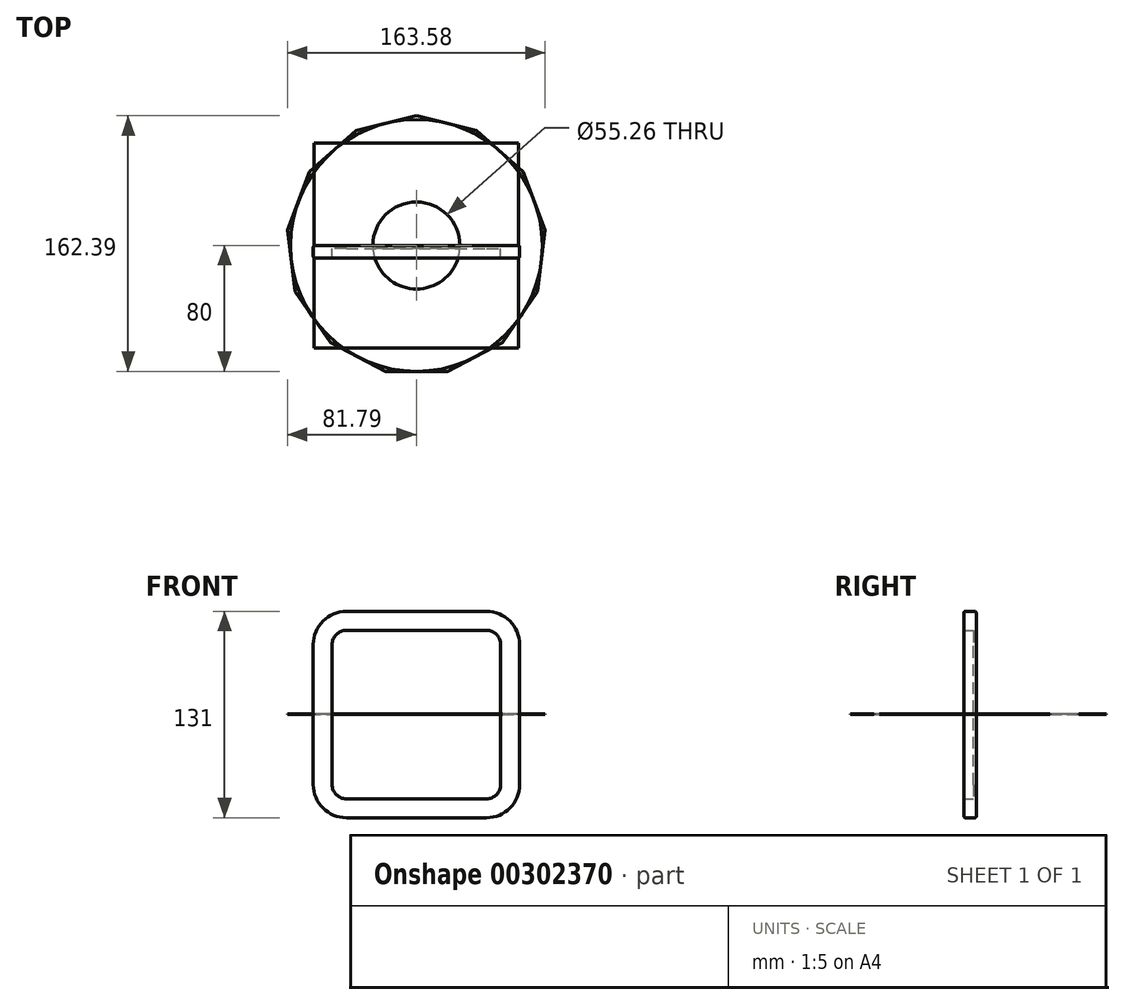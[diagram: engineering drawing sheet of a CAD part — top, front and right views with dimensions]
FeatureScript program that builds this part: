
annotation { "Feature Type Name" : "Feature", "Feature Type Description" : "" }
export const myFeature = defineFeature(function(context is Context, id is Id, definition is map)
    precondition{}
    {
        {
            var Q0;
            Q0=qCreatedBy(makeId("Front.planeOp"),FACE);
            var sketch = newSketch(context, id + "F0", { "sketchPlane" : qUnion([Q0])});
            skLineSegment(sketch, "E0.bottom", {"start": v(44.5, 53.5) * mm, "end": v(-44.5, 53.5) * mm});
            skLineSegment(sketch, "E0.top", {"start": v(44.5, -53.5) * mm, "end": v(-44.5, -53.5) * mm});
            skLineSegment(sketch, "E0.left", {"start": v(53.5, 44.5) * mm, "end": v(53.5, -44.5) * mm});
            skLineSegment(sketch, "E0.right", {"start": v(-53.5, 44.5) * mm, "end": v(-53.5, -44.5) * mm});
            skPoint(sketch, "E0.middle", {"position": v(0, 0) * mm});
            skPoint(sketch, "E1.visualSharp", {"position": v(-53.5, 53.5) * mm});
            skArc(sketch, "E1.filletArc", {"start": v(-44.5, 53.5) * mm, "mid": v(-50.86, 50.86) * mm, "end": v(-53.5, 44.5) * mm});
            skPoint(sketch, "E2.visualSharp", {"position": v(53.5, 53.5) * mm});
            skArc(sketch, "E2.filletArc", {"start": v(53.5, 44.5) * mm, "mid": v(50.86, 50.86) * mm, "end": v(44.5, 53.5) * mm});
            skPoint(sketch, "E3.visualSharp", {"position": v(-53.5, -53.5) * mm});
            skArc(sketch, "E3.filletArc", {"start": v(-53.5, -44.5) * mm, "mid": v(-50.86, -50.86) * mm, "end": v(-44.5, -53.5) * mm});
            skPoint(sketch, "E4.visualSharp", {"position": v(53.5, -53.5) * mm});
            skArc(sketch, "E4.filletArc", {"start": v(44.5, -53.5) * mm, "mid": v(50.86, -50.86) * mm, "end": v(53.5, -44.5) * mm});
            skLineSegment(sketch, "E5.0", {"start": v(65.5, 44.5) * mm, "end": v(65.5, -44.5) * mm});
            skArc(sketch, "E5.1", {"start": v(44.5, -65.5) * mm, "mid": v(59.35, -59.35) * mm, "end": v(65.5, -44.5) * mm});
            skArc(sketch, "E5.2", {"start": v(65.5, 44.5) * mm, "mid": v(59.35, 59.35) * mm, "end": v(44.5, 65.5) * mm});
            skLineSegment(sketch, "E5.3", {"start": v(44.5, -65.5) * mm, "end": v(-44.5, -65.5) * mm});
            skLineSegment(sketch, "E5.4", {"start": v(44.5, 65.5) * mm, "end": v(-44.5, 65.5) * mm});
            skArc(sketch, "E5.5", {"start": v(-44.5, 65.5) * mm, "mid": v(-59.35, 59.35) * mm, "end": v(-65.5, 44.5) * mm});
            skLineSegment(sketch, "E5.6", {"start": v(-65.5, 44.5) * mm, "end": v(-65.5, -44.5) * mm});
            skArc(sketch, "E5.7", {"start": v(-65.5, -44.5) * mm, "mid": v(-59.35, -59.35) * mm, "end": v(-44.5, -65.5) * mm});
            skSolve(sketch);
        }
        {
            var Q0;
            Q0 = qSketchRegion(id + "F0", true);
            var Q1;
            Q1=makeQuery(id+"F0.imprint","IMPRINT",FACE,{"disambiguationData":[TD([[makeQuery(id+"F0.imprint","IMPRINT",EDGE,{"derivedFrom":sQuery(id+"F0.wireOp",EDGE,"E0.bottom")}),1.0]])]});
            extrude(context, id + "F1", {"entities" : qUnion([Q0, Q1]), "depth" : 2 * mm});
        }
        {
            var Q0;
            Q0=makeQuery(id+"F0.imprint","IMPRINT",FACE,{"disambiguationData":[TD([[makeQuery(id+"F0.imprint","IMPRINT",EDGE,{"derivedFrom":sQuery(id+"F0.wireOp",EDGE,"E0.bottom")}),-1.0]])]});
            extrude(context, id + "F2", {"entities" : qUnion([Q0]), "operationType" : NewBodyOperationType.ADD, "depth" : 8 * mm});
        }
        {
            var Q0;
            Q0=makeQuery(id+"F1.opExtrude","CAP_EDGE",EDGE,{"disambiguationData":[OSD([sQuery(id+"F0.wireOp",EDGE,"E5.3")])],"isStart":true});
            var Q1;
            Q1=makeQuery(id+"F2.opExtrude","CAP_EDGE",EDGE,{"disambiguationData":[OSD([sQuery(id+"F0.wireOp",EDGE,"E5.3")])],"isStart":false});
            fillet(context, id + "F3", {"entities" : qUnion([Q0, Q1]), "radius" : 1 * mm, "tangentPropagation" : true, "allowEdgeOverflow" : false});
        }
        {
            var Q0;
            Q0=qCreatedBy(makeId("Top.planeOp"),FACE);
            var sketch = newSketch(context, id + "F4", { "sketchPlane" : qUnion([Q0])});
            skCircle(sketch, "E6.cCircle", {"center": v(0, 0) * mm, "radius": 80 * mm, "construction": true});
            skLineSegment(sketch, "E6.0", {"start": v(38.3, 72.96) * mm, "end": v(67.8, 46.8) * mm});
            skLineSegment(sketch, "E6.1", {"start": v(67.8, 46.8) * mm, "end": v(81.8, 9.93) * mm});
            skLineSegment(sketch, "E6.2", {"start": v(81.8, 9.93) * mm, "end": v(77.04, -29.22) * mm});
            skLineSegment(sketch, "E6.3", {"start": v(77.04, -29.22) * mm, "end": v(54.64, -61.67) * mm});
            skLineSegment(sketch, "E6.4", {"start": v(54.64, -61.67) * mm, "end": v(19.72, -80) * mm});
            skLineSegment(sketch, "E6.5", {"start": v(19.72, -80) * mm, "end": v(-19.72, -80) * mm});
            skLineSegment(sketch, "E6.6", {"start": v(-19.72, -80) * mm, "end": v(-54.64, -61.67) * mm});
            skLineSegment(sketch, "E6.7", {"start": v(-54.64, -61.67) * mm, "end": v(-77.04, -29.22) * mm});
            skLineSegment(sketch, "E6.8", {"start": v(-77.04, -29.22) * mm, "end": v(-81.8, 9.93) * mm});
            skLineSegment(sketch, "E6.9", {"start": v(-81.8, 9.93) * mm, "end": v(-67.8, 46.8) * mm});
            skLineSegment(sketch, "E6.10", {"start": v(-67.8, 46.8) * mm, "end": v(-38.3, 72.96) * mm});
            skLineSegment(sketch, "E6.11", {"start": v(-38.3, 72.96) * mm, "end": v(0, 82.4) * mm});
            skLineSegment(sketch, "E6.12", {"start": v(0, 82.4) * mm, "end": v(38.3, 72.96) * mm});
            skPoint(sketch, "E6.0.midPoint", {"position": v(53.05, 59.88) * mm});
            skSolve(sketch);
        }
        {
            var Q0;
            Q0 = qSketchRegion(id + "F4", true);
            extrude(context, id + "F5", {"entities" : qUnion([Q0]), "depth" : .3 * mm, "offsetDistance" : 25 * mm});
        }
        {
            var Q0;
            Q0=makeQuery(id+"F5.opExtrude","CAP_FACE",FACE,{"disambiguationData":[OSD([sQuery(id+"F4.wireOp",EDGE,"E6.0"),sQuery(id+"F4.wireOp",EDGE,"E6.1"),sQuery(id+"F4.wireOp",EDGE,"E6.2"),sQuery(id+"F4.wireOp",EDGE,"E6.3"),sQuery(id+"F4.wireOp",EDGE,"E6.4"),sQuery(id+"F4.wireOp",EDGE,"E6.5"),sQuery(id+"F4.wireOp",EDGE,"E6.6"),sQuery(id+"F4.wireOp",EDGE,"E6.7"),sQuery(id+"F4.wireOp",EDGE,"E6.8"),sQuery(id+"F4.wireOp",EDGE,"E6.9"),sQuery(id+"F4.wireOp",EDGE,"E6.10"),sQuery(id+"F4.wireOp",EDGE,"E6.11"),sQuery(id+"F4.wireOp",EDGE,"E6.12")])],"isStart":false});
            var sketch = newSketch(context, id + "F6", { "sketchPlane" : qUnion([Q0])});
            skCircle(sketch, "E7", {"center": v(0, 0) * mm, "radius": 27.63 * mm});
            skSolve(sketch);
        }
        {
            var Q0;
            Q0=makeQuery(id+"F6.imprint","IMPRINT",FACE,{"disambiguationData":[TD([[makeQuery(id+"F6.imprint","IMPRINT",EDGE,{"derivedFrom":sQuery(id+"F6.wireOp",EDGE,"E7")}),1.0]])]});
            extrude(context, id + "F7", {"entities" : qUnion([Q0]), "operationType" : NewBodyOperationType.REMOVE, "oppositeDirection" : true, "depth" : .3 * mm, "offsetDistance" : 25 * mm});
        }
        {
            var Q0;
            Q0=qCreatedBy(makeId("Top.planeOp"),FACE);
            var sketch = newSketch(context, id + "F8", { "sketchPlane" : qUnion([Q0])});
            skCircle(sketch, "E8", {"center": v(0, 0) * mm, "radius": 80 * mm});
            skSolve(sketch);
        }
        {
            var Q0;
            Q0=makeQuery(id+"F8.imprint","IMPRINT",FACE,{"disambiguationData":[TD([[makeQuery(id+"F8.imprint","IMPRINT",EDGE,{"derivedFrom":sQuery(id+"F8.wireOp",EDGE,"E8")}),1.0]])]});
            extrude(context, id + "F9", {"entities" : qUnion([Q0]), "depth" : .3 * mm, "offsetDistance" : 25 * mm});
        }
        {
            var Q0;
            Q0=qCreatedBy(makeId("Top.planeOp"),FACE);
            var sketch = newSketch(context, id + "F10", { "sketchPlane" : qUnion([Q0])});
            skLineSegment(sketch, "E9.bottom", {"start": v(65, 65) * mm, "end": v(-65, 65) * mm});
            skLineSegment(sketch, "E9.top", {"start": v(65, -65) * mm, "end": v(-65, -65) * mm});
            skLineSegment(sketch, "E9.left", {"start": v(65, 65) * mm, "end": v(65, -65) * mm});
            skLineSegment(sketch, "E9.right", {"start": v(-65, 65) * mm, "end": v(-65, -65) * mm});
            skPoint(sketch, "E9.middle", {"position": v(0, 0) * mm});
            skCircle(sketch, "E10", {"center": v(0, 0) * mm, "radius": 80 * mm, "construction": true});
            skSolve(sketch);
        }
        {
            var Q0;
            Q0=makeQuery(id+"F10.imprint","IMPRINT",FACE,{"disambiguationData":[TD([[makeQuery(id+"F10.imprint","IMPRINT",EDGE,{"derivedFrom":sQuery(id+"F10.wireOp",EDGE,"E9.bottom")}),1.0]])]});
            extrude(context, id + "F11", {"entities" : qUnion([Q0]), "depth" : .3 * mm, "offsetDistance" : 25 * mm});
        }
    });
